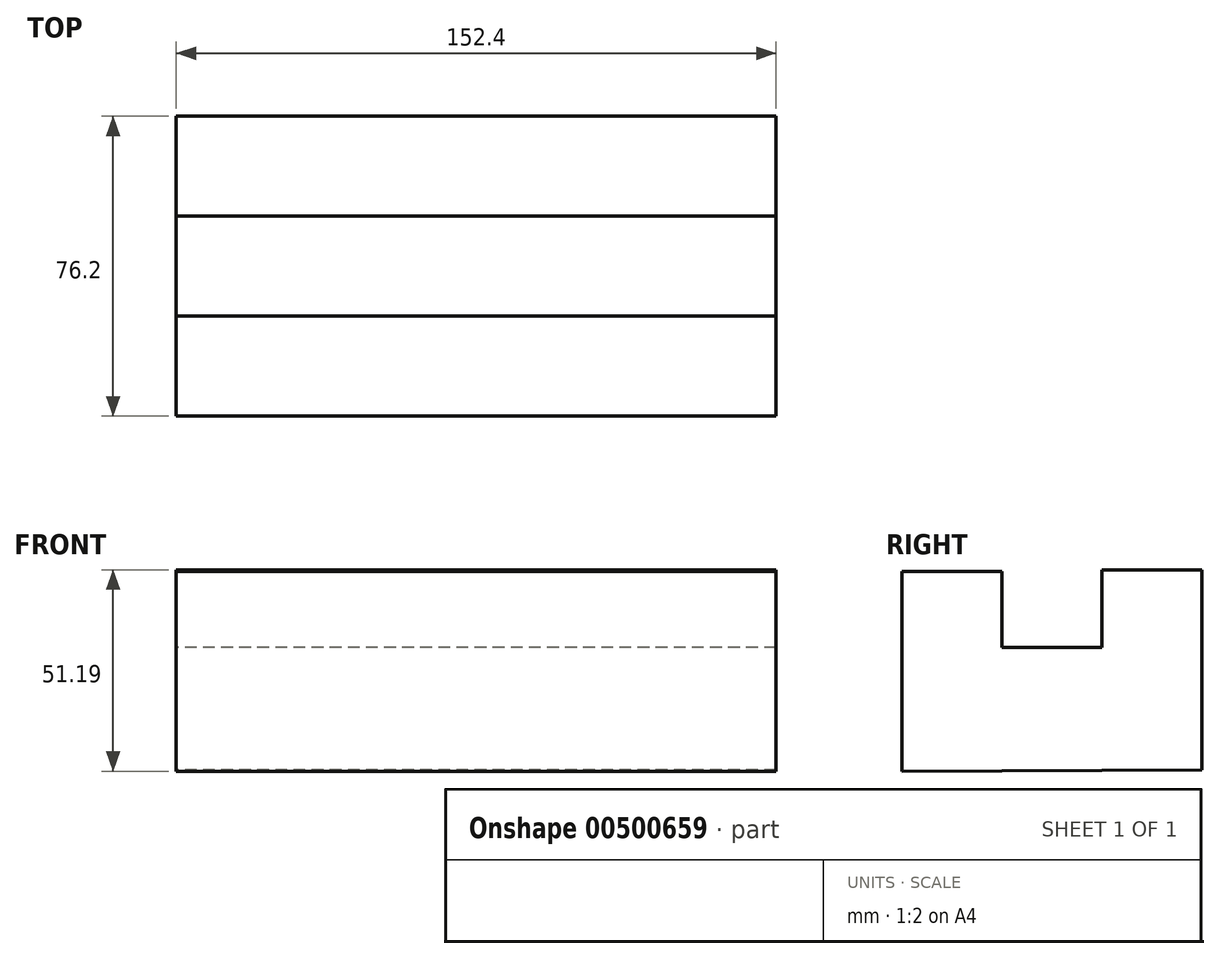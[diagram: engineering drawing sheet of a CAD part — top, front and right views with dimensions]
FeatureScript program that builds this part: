
annotation { "Feature Type Name" : "Feature", "Feature Type Description" : "" }
export const myFeature = defineFeature(function(context is Context, id is Id, definition is map)
    precondition{}
    {
        {
            var Q0;
            Q0=qCreatedBy(makeId("Right.planeOp"),FACE);
            var sketch = newSketch(context, id + "F0", { "sketchPlane" : qUnion([Q0])});
            skLineSegment(sketch, "E0", {"start": v(-40.92, 36.68) * mm, "end": v(-40.92, -14.12) * mm});
            skLineSegment(sketch, "E1", {"start": v(-40.92, -14.12) * mm, "end": v(35.27, -13.73) * mm});
            skLineSegment(sketch, "E2", {"start": v(35.27, -13.73) * mm, "end": v(35.28, 37.07) * mm});
            skLineSegment(sketch, "E3", {"start": v(35.28, 37.07) * mm, "end": v(9.88, 37.07) * mm});
            skLineSegment(sketch, "E4", {"start": v(9.88, 37.07) * mm, "end": v(9.88, 17.33) * mm});
            skLineSegment(sketch, "E5", {"start": v(-40.92, 36.68) * mm, "end": v(-15.52, 36.68) * mm});
            skLineSegment(sketch, "E6", {"start": v(-15.52, 36.68) * mm, "end": v(-15.52, 17.33) * mm});
            skLineSegment(sketch, "E7", {"start": v(-15.52, 17.33) * mm, "end": v(9.88, 17.33) * mm});
            skSolve(sketch);
        }
        {
            var Q0;
            Q0 = qSketchRegion(id + "F0", true);
            extrude(context, id + "F1", {"entities" : qUnion([Q0]), "depth" : 152.4 * mm});
        }
    });
